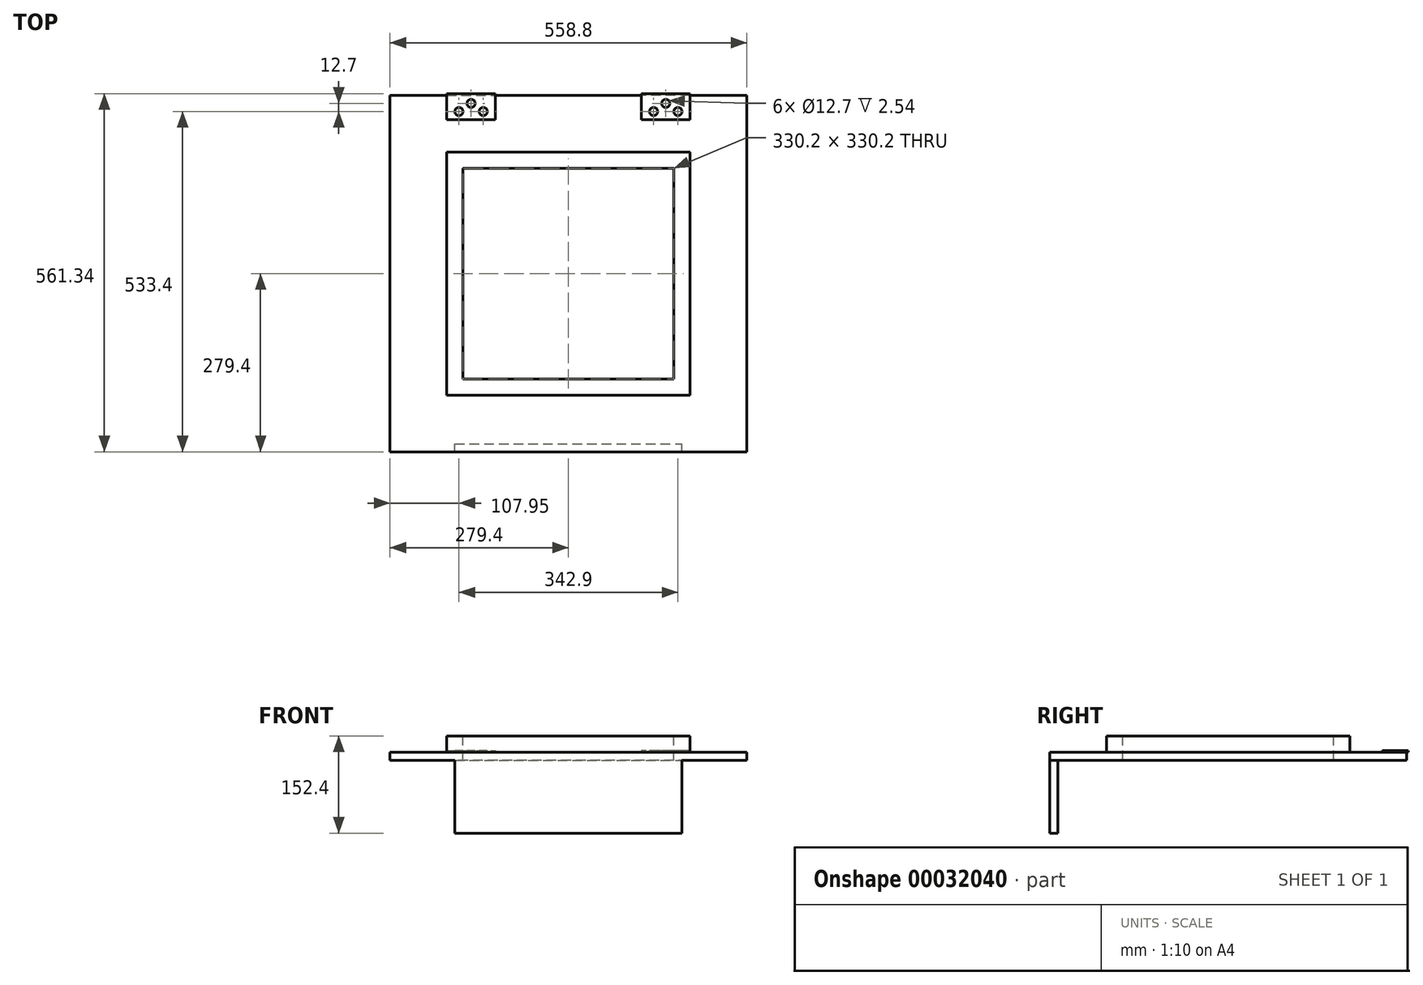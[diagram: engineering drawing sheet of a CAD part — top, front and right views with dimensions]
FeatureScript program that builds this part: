
annotation { "Feature Type Name" : "Feature", "Feature Type Description" : "" }
export const myFeature = defineFeature(function(context is Context, id is Id, definition is map)
    precondition{}
    {
        {
            var Q0;
            Q0=qCreatedBy(makeId("Top.planeOp"),FACE);
            var sketch = newSketch(context, id + "F0", { "sketchPlane" : qUnion([Q0])});
            skLineSegment(sketch, "E0.rect.bottom", {"start": v(279.4, 279.4) * mm, "end": v(-279.4, 279.4) * mm});
            skLineSegment(sketch, "E0.rect.top", {"start": v(279.4, -279.4) * mm, "end": v(-279.4, -279.4) * mm});
            skLineSegment(sketch, "E0.rect.left", {"start": v(279.4, 279.4) * mm, "end": v(279.4, -279.4) * mm});
            skLineSegment(sketch, "E0.rect.right", {"start": v(-279.4, 279.4) * mm, "end": v(-279.4, -279.4) * mm});
            skPoint(sketch, "E0.rect.middle", {"position": v(0, 0) * mm});
            skSolve(sketch);
        }
        {
            var Q0;
            Q0=makeQuery(id+"F0.imprint","IMPRINT",FACE,{"disambiguationData":[TD([[makeQuery(id+"F0.imprint","IMPRINT",EDGE,{"derivedFrom":sQuery(id+"F0.wireOp",EDGE,"E0.rect.bottom")}),1.0]])]});
            extrude(context, id + "F1", {"entities" : qUnion([Q0]), "depth" : 12.7 * mm});
        }
        {
            var Q0;
            Q0=makeQuery(id+"F1.opExtrude","CAP_FACE",FACE,{"disambiguationData":[OSD([sQuery(id+"F0.wireOp",EDGE,"E0.rect.bottom"),sQuery(id+"F0.wireOp",EDGE,"E0.rect.top"),sQuery(id+"F0.wireOp",EDGE,"E0.rect.left"),sQuery(id+"F0.wireOp",EDGE,"E0.rect.right")])],"isStart":true});
            var sketch = newSketch(context, id + "F2", { "sketchPlane" : qUnion([Q0])});
            skLineSegment(sketch, "E1.bottom", {"start": v(-279.4, 279.4) * mm, "end": v(-177.8, 279.4) * mm});
            skLineSegment(sketch, "E1.top", {"start": v(-279.4, 266.7) * mm, "end": v(-177.8, 266.7) * mm});
            skLineSegment(sketch, "E1.left", {"start": v(-279.4, 279.4) * mm, "end": v(-279.4, 266.7) * mm});
            skLineSegment(sketch, "E1.right", {"start": v(-177.8, 279.4) * mm, "end": v(-177.8, 266.7) * mm});
            skLineSegment(sketch, "E2.bottom", {"start": v(279.4, 279.4) * mm, "end": v(177.8, 279.4) * mm});
            skLineSegment(sketch, "E2.top", {"start": v(279.4, 266.7) * mm, "end": v(177.8, 266.7) * mm});
            skLineSegment(sketch, "E2.left", {"start": v(279.4, 279.4) * mm, "end": v(279.4, 266.7) * mm});
            skLineSegment(sketch, "E2.right", {"start": v(177.8, 279.4) * mm, "end": v(177.8, 266.7) * mm});
            skLineSegment(sketch, "E3.bottom", {"start": v(-177.8, 266.7) * mm, "end": v(177.8, 266.7) * mm});
            skLineSegment(sketch, "E3.top", {"start": v(-177.8, 279.4) * mm, "end": v(177.8, 279.4) * mm});
            skLineSegment(sketch, "E3.left", {"start": v(-177.8, 266.7) * mm, "end": v(-177.8, 279.4) * mm});
            skLineSegment(sketch, "E3.right", {"start": v(177.8, 266.7) * mm, "end": v(177.8, 279.4) * mm});
            skSolve(sketch);
        }
        {
            var Q0;
            Q0=makeQuery(id+"F2.imprint","IMPRINT",FACE,{"disambiguationData":[TD([[makeQuery(id+"F2.imprint","IMPRINT",EDGE,{"derivedFrom":sQuery(id+"F2.wireOp",EDGE,"E3.bottom")}),1.0]])]});
            extrude(context, id + "F3", {"entities" : qUnion([Q0]), "operationType" : NewBodyOperationType.ADD, "depth" : 114.3 * mm});
        }
        {
            var Q0;
            Q0=makeQuery(id+"F1.opExtrude","CAP_FACE",FACE,{"disambiguationData":[OSD([sQuery(id+"F0.wireOp",EDGE,"E0.rect.bottom"),sQuery(id+"F0.wireOp",EDGE,"E0.rect.top"),sQuery(id+"F0.wireOp",EDGE,"E0.rect.left"),sQuery(id+"F0.wireOp",EDGE,"E0.rect.right")])],"isStart":false});
            var sketch = newSketch(context, id + "F4", { "sketchPlane" : qUnion([Q0])});
            skLineSegment(sketch, "E4.rect.bottom", {"start": v(165.1, 165.1) * mm, "end": v(-165.1, 165.1) * mm});
            skLineSegment(sketch, "E4.rect.top", {"start": v(165.1, -165.1) * mm, "end": v(-165.1, -165.1) * mm});
            skLineSegment(sketch, "E4.rect.left", {"start": v(165.1, 165.1) * mm, "end": v(165.1, -165.1) * mm});
            skLineSegment(sketch, "E4.rect.right", {"start": v(-165.1, 165.1) * mm, "end": v(-165.1, -165.1) * mm});
            skPoint(sketch, "E4.rect.middle", {"position": v(0, 0) * mm});
            skSolve(sketch);
        }
        {
            var Q0;
            Q0=makeQuery(id+"F4.imprint","IMPRINT",FACE,{"disambiguationData":[TD([[makeQuery(id+"F4.imprint","IMPRINT",EDGE,{"derivedFrom":sQuery(id+"F4.wireOp",EDGE,"E4.rect.bottom")}),1.0]])]});
            extrude(context, id + "F5", {"entities" : qUnion([Q0]), "operationType" : NewBodyOperationType.REMOVE, "oppositeDirection" : true, "depth" : 25.4 * mm});
        }
        {
            var Q0;
            Q0=makeQuery(id+"F1.opExtrude","CAP_FACE",FACE,{"disambiguationData":[OSD([sQuery(id+"F0.wireOp",EDGE,"E0.rect.bottom"),sQuery(id+"F0.wireOp",EDGE,"E0.rect.top"),sQuery(id+"F0.wireOp",EDGE,"E0.rect.left"),sQuery(id+"F0.wireOp",EDGE,"E0.rect.right")])],"isStart":false});
            var sketch = newSketch(context, id + "F6", { "sketchPlane" : qUnion([Q0])});
            skLineSegment(sketch, "E5.rect.bottom", {"start": v(190.5, 190.5) * mm, "end": v(-190.5, 190.5) * mm});
            skLineSegment(sketch, "E5.rect.top", {"start": v(190.5, -190.5) * mm, "end": v(-190.5, -190.5) * mm});
            skLineSegment(sketch, "E5.rect.left", {"start": v(190.5, 190.5) * mm, "end": v(190.5, -190.5) * mm});
            skLineSegment(sketch, "E5.rect.right", {"start": v(-190.5, 190.5) * mm, "end": v(-190.5, -190.5) * mm});
            skPoint(sketch, "E5.rect.middle", {"position": v(0, 0) * mm});
            skSolve(sketch);
        }
        {
            var Q0;
            Q0=makeQuery(id+"F6.imprint","IMPRINT",FACE,{"disambiguationData":[TD([[makeQuery(id+"F6.imprint","IMPRINT",EDGE,{"derivedFrom":sQuery(id+"F6.wireOp",EDGE,"E5.rect.bottom")}),1.0]])]});
            extrude(context, id + "F7", {"entities" : qUnion([Q0]), "operationType" : NewBodyOperationType.ADD, "depth" : 25.4 * mm});
        }
        {
            var Q0;
            Q0=makeQuery(id+"F1.opExtrude","CAP_FACE",FACE,{"disambiguationData":[OSD([sQuery(id+"F0.wireOp",EDGE,"E0.rect.bottom"),sQuery(id+"F0.wireOp",EDGE,"E0.rect.top"),sQuery(id+"F0.wireOp",EDGE,"E0.rect.left"),sQuery(id+"F0.wireOp",EDGE,"E0.rect.right")])],"isStart":false});
            var sketch = newSketch(context, id + "F8", { "sketchPlane" : qUnion([Q0])});
            skLineSegment(sketch, "E6", {"start": v(-279.4, 279.4) * mm, "end": v(-190.5, 279.4) * mm});
            skLineSegment(sketch, "E7", {"start": v(279.4, 279.4) * mm, "end": v(190.5, 279.4) * mm});
            skLineSegment(sketch, "E8.bottom", {"start": v(-190.5, 279.4) * mm, "end": v(-114.3, 279.4) * mm});
            skLineSegment(sketch, "E8.top", {"start": v(-190.5, 241.3) * mm, "end": v(-114.3, 241.3) * mm});
            skLineSegment(sketch, "E8.left", {"start": v(-190.5, 279.4) * mm, "end": v(-190.5, 241.3) * mm});
            skLineSegment(sketch, "E8.right", {"start": v(-114.3, 279.4) * mm, "end": v(-114.3, 241.3) * mm});
            skLineSegment(sketch, "E9.bottom", {"start": v(190.5, 279.4) * mm, "end": v(114.3, 279.4) * mm});
            skLineSegment(sketch, "E9.top", {"start": v(190.5, 241.3) * mm, "end": v(114.3, 241.3) * mm});
            skLineSegment(sketch, "E9.left", {"start": v(190.5, 279.4) * mm, "end": v(190.5, 241.3) * mm});
            skLineSegment(sketch, "E9.right", {"start": v(114.3, 279.4) * mm, "end": v(114.3, 241.3) * mm});
            skSolve(sketch);
        }
        {
            var Q0;
            Q0=makeQuery(id+"F8.imprint","IMPRINT",FACE,{"disambiguationData":[TD([[makeQuery(id+"F8.imprint","IMPRINT",EDGE,{"derivedFrom":sQuery(id+"F8.wireOp",EDGE,"E8.bottom")}),1.0]])]});
            var Q1;
            Q1=makeQuery(id+"F8.imprint","IMPRINT",FACE,{"disambiguationData":[TD([[makeQuery(id+"F8.imprint","IMPRINT",EDGE,{"derivedFrom":sQuery(id+"F8.wireOp",EDGE,"E9.bottom")}),1.0]])]});
            extrude(context, id + "F9", {"entities" : qUnion([Q0, Q1]), "operationType" : NewBodyOperationType.ADD, "depth" : 2.54 * mm});
        }
        {
            var Q0;
            Q0=makeQuery(id+"F9.boolean.opBoolean","MERGE",FACE,{"derivedFrom":[makeQuery(id+"F1.opExtrude","SWEPT_FACE",FACE,{"disambiguationData":[OSD([sQuery(id+"F0.wireOp",EDGE,"E0.rect.bottom")])]}),makeQuery(id+"F9.opExtrude","SWEPT_FACE",FACE,{"disambiguationData":[OSD([sQuery(id+"F8.wireOp",EDGE,"E8.bottom")])]}),makeQuery(id+"F9.opExtrude","SWEPT_FACE",FACE,{"disambiguationData":[OSD([sQuery(id+"F8.wireOp",EDGE,"E9.bottom")])]})]});
            var sketch = newSketch(context, id + "F10", { "sketchPlane" : qUnion([Q0])});
            skLineSegment(sketch, "E10.bottom", {"start": v(-190.5, 15.24) * mm, "end": v(-114.3, 15.24) * mm});
            skLineSegment(sketch, "E10.top", {"start": v(-190.5, 12.7) * mm, "end": v(-114.3, 12.7) * mm});
            skLineSegment(sketch, "E10.left", {"start": v(-190.5, 15.24) * mm, "end": v(-190.5, 12.7) * mm});
            skLineSegment(sketch, "E10.right", {"start": v(-114.3, 15.24) * mm, "end": v(-114.3, 12.7) * mm});
            skLineSegment(sketch, "E11.bottom", {"start": v(190.5, 15.24) * mm, "end": v(114.3, 15.24) * mm});
            skLineSegment(sketch, "E11.top", {"start": v(190.5, 12.7) * mm, "end": v(114.3, 12.7) * mm});
            skLineSegment(sketch, "E11.left", {"start": v(190.5, 15.24) * mm, "end": v(190.5, 12.7) * mm});
            skLineSegment(sketch, "E11.right", {"start": v(114.3, 15.24) * mm, "end": v(114.3, 12.7) * mm});
            skSolve(sketch);
        }
        {
            var Q0;
            Q0 = qSketchRegion(id + "F10", true);
            extrude(context, id + "F11", {"entities" : qUnion([Q0]), "operationType" : NewBodyOperationType.ADD, "depth" : 2.54 * mm});
        }
        {
            var Q0;
            Q0=makeQuery(id+"F11.boolean.opBoolean","MERGE",FACE,{"derivedFrom":[makeQuery(id+"F9.opExtrude","CAP_FACE",FACE,{"disambiguationData":[OSD([sQuery(id+"F8.wireOp",EDGE,"E8.bottom"),sQuery(id+"F8.wireOp",EDGE,"E8.top"),sQuery(id+"F8.wireOp",EDGE,"E8.left"),sQuery(id+"F8.wireOp",EDGE,"E8.right")])],"isStart":false}),makeQuery(id+"F11.opExtrude","SWEPT_FACE",FACE,{"disambiguationData":[OSD([sQuery(id+"F10.wireOp",EDGE,"E11.bottom")])]})]});
            var sketch = newSketch(context, id + "F12", { "sketchPlane" : qUnion([Q0])});
            skLineSegment(sketch, "E12", {"start": v(-152.4, 241.3) * mm, "end": v(-152.4, 266.7) * mm});
            skLineSegment(sketch, "E13", {"start": v(-152.4, 266.7) * mm, "end": v(-114.3, 266.7) * mm});
            skLineSegment(sketch, "E14", {"start": v(-152.4, 266.7) * mm, "end": v(-190.5, 266.7) * mm});
            skLineSegment(sketch, "E15", {"start": v(-171.45, 266.7) * mm, "end": v(-171.45, 241.3) * mm});
            skLineSegment(sketch, "E16", {"start": v(-133.35, 266.7) * mm, "end": v(-133.35, 241.3) * mm});
            skCircle(sketch, "E17", {"center": v(-152.4, 266.7) * mm, "radius": 6.35 * mm});
            skCircle(sketch, "E18", {"center": v(-171.45, 254) * mm, "radius": 6.35 * mm});
            skCircle(sketch, "E19", {"center": v(-133.35, 254) * mm, "radius": 6.35 * mm});
            skSolve(sketch);
        }
        {
            var Q0;
            {var subQ1=sQuery(id+"F12.wireOp",EDGE,"E13");var subQ3=sQuery(id+"F12.wireOp",EDGE,"E17");var subQ4=makeQuery(id+"F12.imprint","INTERSECT",VERTEX,{"derivedFrom":[subQ1,subQ3]});Q0=makeQuery(id+"F12.imprint","IMPRINT",FACE,{"disambiguationData":[TD([[makeQuery(id+"F12.imprint","IMPRINT",EDGE,{"disambiguationData":[TD([[subQ4,-1.0]])],"derivedFrom":subQ3}),1.0]])]});}
            var Q1;
            {var subQ1=sQuery(id+"F12.wireOp",EDGE,"E12");var subQ3=sQuery(id+"F12.wireOp",EDGE,"E17");var subQ4=makeQuery(id+"F12.imprint","INTERSECT",VERTEX,{"derivedFrom":[subQ1,subQ3]});Q1=makeQuery(id+"F12.imprint","IMPRINT",FACE,{"disambiguationData":[TD([[makeQuery(id+"F12.imprint","IMPRINT",EDGE,{"disambiguationData":[TD([[subQ4,1.0]])],"derivedFrom":subQ3}),1.0]])]});}
            var Q2;
            {var subQ1=sQuery(id+"F12.wireOp",EDGE,"E12");var subQ3=sQuery(id+"F12.wireOp",EDGE,"E17");var subQ4=makeQuery(id+"F12.imprint","INTERSECT",VERTEX,{"derivedFrom":[subQ1,subQ3]});Q2=makeQuery(id+"F12.imprint","IMPRINT",FACE,{"disambiguationData":[TD([[makeQuery(id+"F12.imprint","IMPRINT",EDGE,{"disambiguationData":[TD([[subQ4,-1.0]])],"derivedFrom":subQ3}),1.0]])]});}
            var Q3;
            {var subQ0=sQuery(id+"F12.wireOp",EDGE,"E18");var subQ1=sQuery(id+"F12.wireOp",EDGE,"E15");var subQ2=makeQuery(id+"F12.imprint","INTERSECT",VERTEX,{"disambiguationData":[OD(0.0)],"derivedFrom":[subQ1,subQ0]});Q3=makeQuery(id+"F12.imprint","IMPRINT",FACE,{"disambiguationData":[TD([[makeQuery(id+"F12.imprint","IMPRINT",EDGE,{"disambiguationData":[TD([[subQ2,-1.0]])],"derivedFrom":subQ1}),-1.0]])]});}
            var Q4;
            {var subQ0=sQuery(id+"F12.wireOp",EDGE,"E18");var subQ1=sQuery(id+"F12.wireOp",EDGE,"E15");var subQ2=makeQuery(id+"F12.imprint","INTERSECT",VERTEX,{"disambiguationData":[OD(0.0)],"derivedFrom":[subQ1,subQ0]});Q4=makeQuery(id+"F12.imprint","IMPRINT",FACE,{"disambiguationData":[TD([[makeQuery(id+"F12.imprint","IMPRINT",EDGE,{"disambiguationData":[TD([[subQ2,-1.0]])],"derivedFrom":subQ1}),1.0]])]});}
            var Q5;
            {var subQ0=sQuery(id+"F12.wireOp",EDGE,"E19");var subQ1=sQuery(id+"F12.wireOp",EDGE,"E16");var subQ2=makeQuery(id+"F12.imprint","INTERSECT",VERTEX,{"disambiguationData":[OD(0.0)],"derivedFrom":[subQ1,subQ0]});Q5=makeQuery(id+"F12.imprint","IMPRINT",FACE,{"disambiguationData":[TD([[makeQuery(id+"F12.imprint","IMPRINT",EDGE,{"disambiguationData":[TD([[subQ2,-1.0]])],"derivedFrom":subQ1}),-1.0]])]});}
            var Q6;
            {var subQ0=sQuery(id+"F12.wireOp",EDGE,"E19");var subQ1=sQuery(id+"F12.wireOp",EDGE,"E16");var subQ2=makeQuery(id+"F12.imprint","INTERSECT",VERTEX,{"disambiguationData":[OD(0.0)],"derivedFrom":[subQ1,subQ0]});Q6=makeQuery(id+"F12.imprint","IMPRINT",FACE,{"disambiguationData":[TD([[makeQuery(id+"F12.imprint","IMPRINT",EDGE,{"disambiguationData":[TD([[subQ2,-1.0]])],"derivedFrom":subQ1}),1.0]])]});}
            extrude(context, id + "F13", {"entities" : qUnion([Q0, Q1, Q2, Q3, Q4, Q5, Q6]), "operationType" : NewBodyOperationType.REMOVE, "oppositeDirection" : true, "depth" : 2.54 * mm});
        }
        {
            var Q0;
            Q0=makeQuery(id+"F11.boolean.opBoolean","MERGE",FACE,{"derivedFrom":[makeQuery(id+"F9.opExtrude","CAP_FACE",FACE,{"disambiguationData":[OSD([sQuery(id+"F8.wireOp",EDGE,"E9.bottom"),sQuery(id+"F8.wireOp",EDGE,"E9.top"),sQuery(id+"F8.wireOp",EDGE,"E9.left"),sQuery(id+"F8.wireOp",EDGE,"E9.right")])],"isStart":false}),makeQuery(id+"F11.opExtrude","SWEPT_FACE",FACE,{"disambiguationData":[OSD([sQuery(id+"F10.wireOp",EDGE,"E10.bottom")])]})]});
            var sketch = newSketch(context, id + "F14", { "sketchPlane" : qUnion([Q0])});
            skLineSegment(sketch, "E20", {"start": v(152.4, 241.3) * mm, "end": v(152.4, 266.7) * mm});
            skLineSegment(sketch, "E21", {"start": v(152.4, 266.7) * mm, "end": v(114.3, 266.7) * mm});
            skLineSegment(sketch, "E22", {"start": v(114.3, 266.7) * mm, "end": v(152.4, 266.7) * mm});
            skLineSegment(sketch, "E23", {"start": v(152.4, 266.7) * mm, "end": v(190.5, 266.7) * mm});
            skLineSegment(sketch, "E24", {"start": v(133.35, 266.7) * mm, "end": v(133.35, 241.3) * mm});
            skLineSegment(sketch, "E25", {"start": v(171.45, 266.7) * mm, "end": v(171.45, 241.3) * mm});
            skCircle(sketch, "E26", {"center": v(171.45, 254) * mm, "radius": 6.35 * mm});
            skCircle(sketch, "E27", {"center": v(152.4, 266.7) * mm, "radius": 6.35 * mm});
            skCircle(sketch, "E28", {"center": v(133.35, 254) * mm, "radius": 6.35 * mm});
            skSolve(sketch);
        }
        {
            var Q0;
            {var subQ1=sQuery(id+"F14.wireOp",EDGE,"E22");var subQ3=sQuery(id+"F14.wireOp",EDGE,"E27");var subQ4=makeQuery(id+"F14.imprint","INTERSECT",VERTEX,{"derivedFrom":[subQ1,subQ3]});Q0=makeQuery(id+"F14.imprint","IMPRINT",FACE,{"disambiguationData":[TD([[makeQuery(id+"F14.imprint","IMPRINT",EDGE,{"disambiguationData":[TD([[subQ4,1.0]])],"derivedFrom":subQ3}),1.0]])]});}
            var Q1;
            {var subQ1=sQuery(id+"F14.wireOp",EDGE,"E20");var subQ3=sQuery(id+"F14.wireOp",EDGE,"E27");var subQ4=makeQuery(id+"F14.imprint","INTERSECT",VERTEX,{"derivedFrom":[subQ1,subQ3]});Q1=makeQuery(id+"F14.imprint","IMPRINT",FACE,{"disambiguationData":[TD([[makeQuery(id+"F14.imprint","IMPRINT",EDGE,{"disambiguationData":[TD([[subQ4,1.0]])],"derivedFrom":subQ3}),1.0]])]});}
            var Q2;
            {var subQ1=sQuery(id+"F14.wireOp",EDGE,"E20");var subQ3=sQuery(id+"F14.wireOp",EDGE,"E27");var subQ4=makeQuery(id+"F14.imprint","INTERSECT",VERTEX,{"derivedFrom":[subQ1,subQ3]});Q2=makeQuery(id+"F14.imprint","IMPRINT",FACE,{"disambiguationData":[TD([[makeQuery(id+"F14.imprint","IMPRINT",EDGE,{"disambiguationData":[TD([[subQ4,-1.0]])],"derivedFrom":subQ3}),1.0]])]});}
            var Q3;
            {var subQ0=sQuery(id+"F14.wireOp",EDGE,"E26");var subQ1=sQuery(id+"F14.wireOp",EDGE,"E25");var subQ2=makeQuery(id+"F14.imprint","INTERSECT",VERTEX,{"disambiguationData":[OD(0.0)],"derivedFrom":[subQ1,subQ0]});Q3=makeQuery(id+"F14.imprint","IMPRINT",FACE,{"disambiguationData":[TD([[makeQuery(id+"F14.imprint","IMPRINT",EDGE,{"disambiguationData":[TD([[subQ2,-1.0]])],"derivedFrom":subQ1}),-1.0]])]});}
            var Q4;
            {var subQ0=sQuery(id+"F14.wireOp",EDGE,"E26");var subQ1=sQuery(id+"F14.wireOp",EDGE,"E25");var subQ2=makeQuery(id+"F14.imprint","INTERSECT",VERTEX,{"disambiguationData":[OD(0.0)],"derivedFrom":[subQ1,subQ0]});Q4=makeQuery(id+"F14.imprint","IMPRINT",FACE,{"disambiguationData":[TD([[makeQuery(id+"F14.imprint","IMPRINT",EDGE,{"disambiguationData":[TD([[subQ2,-1.0]])],"derivedFrom":subQ1}),1.0]])]});}
            var Q5;
            {var subQ0=sQuery(id+"F14.wireOp",EDGE,"E28");var subQ1=sQuery(id+"F14.wireOp",EDGE,"E24");var subQ2=makeQuery(id+"F14.imprint","INTERSECT",VERTEX,{"disambiguationData":[OD(0.0)],"derivedFrom":[subQ1,subQ0]});Q5=makeQuery(id+"F14.imprint","IMPRINT",FACE,{"disambiguationData":[TD([[makeQuery(id+"F14.imprint","IMPRINT",EDGE,{"disambiguationData":[TD([[subQ2,-1.0]])],"derivedFrom":subQ1}),1.0]])]});}
            var Q6;
            {var subQ0=sQuery(id+"F14.wireOp",EDGE,"E28");var subQ1=sQuery(id+"F14.wireOp",EDGE,"E24");var subQ2=makeQuery(id+"F14.imprint","INTERSECT",VERTEX,{"disambiguationData":[OD(0.0)],"derivedFrom":[subQ1,subQ0]});Q6=makeQuery(id+"F14.imprint","IMPRINT",FACE,{"disambiguationData":[TD([[makeQuery(id+"F14.imprint","IMPRINT",EDGE,{"disambiguationData":[TD([[subQ2,-1.0]])],"derivedFrom":subQ1}),-1.0]])]});}
            extrude(context, id + "F15", {"entities" : qUnion([Q0, Q1, Q2, Q3, Q4, Q5, Q6]), "operationType" : NewBodyOperationType.REMOVE, "oppositeDirection" : true, "depth" : 2.54 * mm});
        }
    });
